# Revit family: Faucet-Lavatory-KOHLER-JULY-K-29929IN
name_source: partatom
category: Plumbing Fixtures
units: mm (PartAtom-declared; Revit-internal decimal feet)

## family parameters
Cut with Voids When Loaded = No
Host = Face
OmniClass Number = 23.31.11.00
Part Type = Normal
Room Calculation Point = No
Round Connector Dimension = Use Diameter
Shared = No

## types (4) — shared parameters
ADA Compliant = No
Assembly Code = D2010
CW Connection = Yes
Cold Water Inlet = Cold Water Inlet
Date Modified = 08/29/2024
Default Elevation = 36"
Drain Included = Yes
Flow Rate = 6 GPM
HW Connection = Yes
Handle Clearance = 4 1/16"
Height = 10 9/16"
Hot Water Inlet = Hot Water Inlet
Length = 4 7/8"
Manufacturer = Kohler Co.
Master Format 2014 = 22 41 39
Master Format 2014 Name = Residential Faucets, Supplies, and Trim
Material = Brass Construction
Pressure = 43.51 psi
Product Name = JULY
Spout Reach = 4 7/8"
URL = https://www.kohler.co.in
Vent Connection = No
Waste Connection = No
Waste Water Outlet = Waste Water Outlet
WaterSense Certified = No
Width = 1 7/8"

## per-type parameters (varying)
| type | Description | Finish | Model | Product Page URL | Type | With Drain |
| With Drain, CP-Polished Chrome | COMFORT HEIGHT TALL LAVATORY WITH DRAIN | Kohler-Metal-CP-Polished_Chrome | K-29929IN-4-CP |  | 1 | Yes |
| Without Drain, CP-Polished Chrome | Comfort Height Tall Single Control Lav Without Drain | Kohler-Metal-CP-Polished_Chrome | K-29929IN-4ND-CP | https://www.kohler.co.in | 2 | No |
| Without Drain, AF-Vibrant French Gold | Comfort Height Tall Single Control Lav Without Drain | Kohler-Metal-AF-Vibrant_French_Gold | K-29929IN-4ND-AF |  | 3 | No |
| Without Drain, BN-Vibrant Brushed Nickel | Comfort Height Tall Single Control Lav Without Drain | Kohler-Metal-BN-Vibrant_Brushed_Nickel | K-29929IN-4ND-BN |  | 4 | No |

## geometry (parser evidence)
native form markers: Sweep x5
no freeform markers — native parametric forms only
